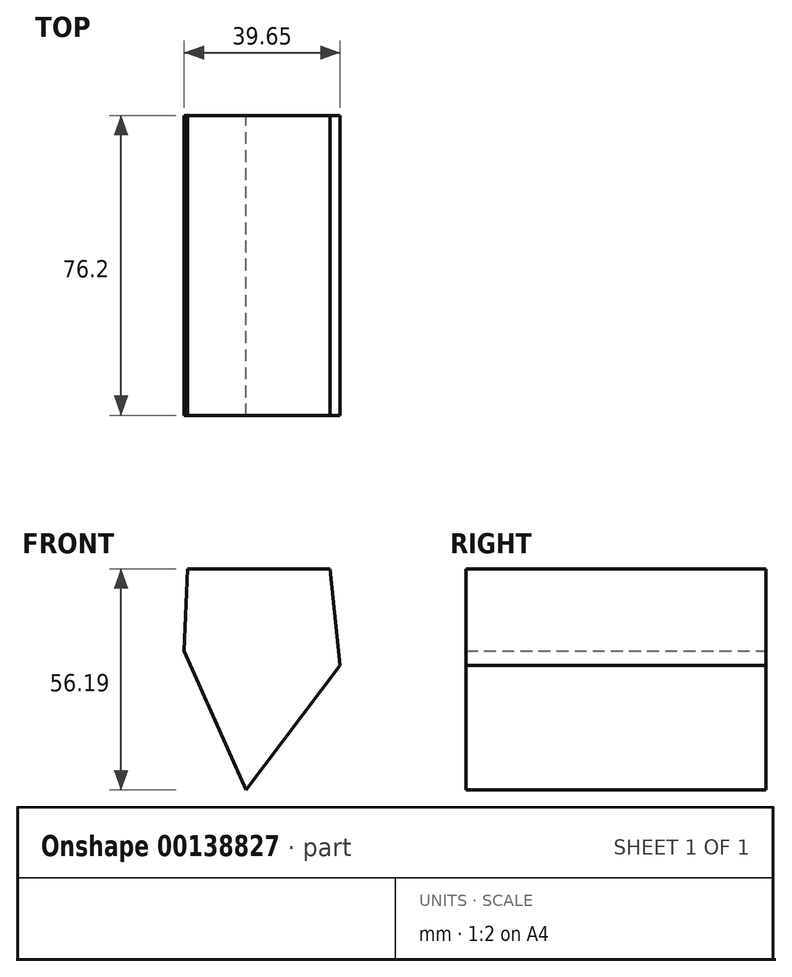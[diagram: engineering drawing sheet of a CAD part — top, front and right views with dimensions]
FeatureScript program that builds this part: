
annotation { "Feature Type Name" : "Feature", "Feature Type Description" : "" }
export const myFeature = defineFeature(function(context is Context, id is Id, definition is map)
    precondition{}
    {
        {
            var Q0;
            Q0=qCreatedBy(makeId("Front.planeOp"),FACE);
            var sketch = newSketch(context, id + "F0", { "sketchPlane" : qUnion([Q0])});
            skLineSegment(sketch, "E0", {"start": v(-62.04, 45.78) * mm, "end": v(-25.81, 45.78) * mm});
            skLineSegment(sketch, "E1", {"start": v(-25.81, 45.78) * mm, "end": v(-23.25, 21.25) * mm});
            skLineSegment(sketch, "E2", {"start": v(-23.25, 21.25) * mm, "end": v(-62.9, 24.96) * mm});
            skLineSegment(sketch, "E3", {"start": v(-62.9, 24.96) * mm, "end": v(-62.04, 45.78) * mm});
            skLineSegment(sketch, "E4", {"start": v(-62.9, 24.96) * mm, "end": v(-47.2, -10.41) * mm});
            skLineSegment(sketch, "E5", {"start": v(-47.2, -10.41) * mm, "end": v(-23.25, 21.25) * mm});
            skLineSegment(sketch, "E6", {"start": v(-62.04, 45.78) * mm, "end": v(-23.25, 21.25) * mm});
            skLineSegment(sketch, "E7", {"start": v(-23.25, 21.25) * mm, "end": v(-55.05, 7.27) * mm});
            skSolve(sketch);
        }
        {
            var Q0;
            Q0 = qSketchRegion(id + "F0", true);
            extrude(context, id + "F1", {"entities" : qUnion([Q0]), "depth" : 76.2 * mm});
        }
    });
